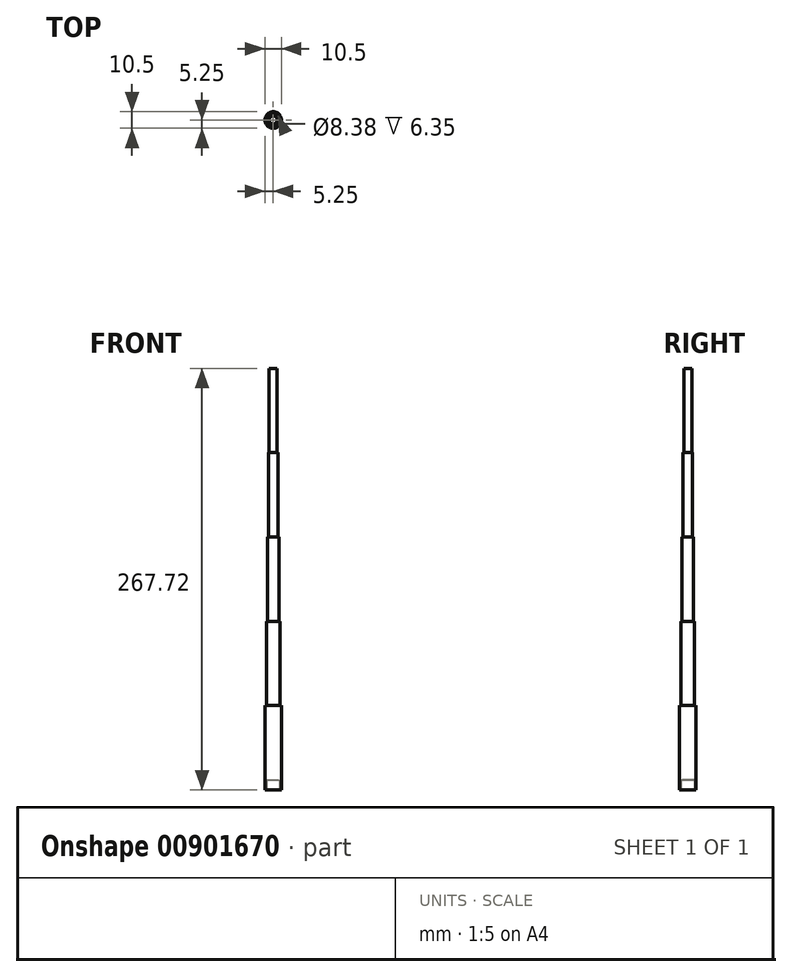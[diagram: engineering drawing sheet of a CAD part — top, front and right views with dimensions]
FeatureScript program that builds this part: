
annotation { "Feature Type Name" : "Feature", "Feature Type Description" : "" }
export const myFeature = defineFeature(function(context is Context, id is Id, definition is map)
    precondition{}
    {
        {
            var Q0;
            Q0=qCreatedBy(makeId("Top.planeOp"),FACE);
            var sketch = newSketch(context, id + "F0", { "sketchPlane" : qUnion([Q0])});
            skCircle(sketch, "E0", {"center": v(0, 0) * mm, "radius": 5.25 * mm});
            skSolve(sketch);
        }
        {
            var Q0;
            Q0=makeQuery(id+"F0.imprint","IMPRINT",FACE,{"disambiguationData":[TD([[makeQuery(id+"F0.imprint","IMPRINT",EDGE,{"derivedFrom":sQuery(id+"F0.wireOp",EDGE,"E0")}),1.0]])]});
            extrude(context, id + "F1", {"entities" : qUnion([Q0]), "depth" : 53.54 * mm, "offsetDistance" : 25.4 * mm});
        }
        {
            var Q0;
            Q0=makeQuery(id+"F1.opExtrude","CAP_FACE",FACE,{"disambiguationData":[OSD([sQuery(id+"F0.wireOp",EDGE,"E0")])],"isStart":true});
            var sketch = newSketch(context, id + "F2", { "sketchPlane" : qUnion([Q0])});
            skCircle(sketch, "E1", {"center": v(0, 0) * mm, "radius": 4.2 * mm});
            skSolve(sketch);
        }
        {
            var Q0;
            Q0=makeQuery(id+"F2.imprint","IMPRINT",FACE,{"disambiguationData":[TD([[makeQuery(id+"F2.imprint","IMPRINT",EDGE,{"derivedFrom":sQuery(id+"F2.wireOp",EDGE,"E1")}),1.0]])]});
            extrude(context, id + "F3", {"entities" : qUnion([Q0]), "operationType" : NewBodyOperationType.REMOVE, "oppositeDirection" : true, "depth" : 6.35 * mm, "offsetDistance" : 25.4 * mm});
        }
        {
            var Q0;
            Q0=makeQuery(id+"F1.opExtrude","CAP_FACE",FACE,{"disambiguationData":[OSD([sQuery(id+"F0.wireOp",EDGE,"E0")])],"isStart":false});
            var sketch = newSketch(context, id + "F4", { "sketchPlane" : qUnion([Q0])});
            skCircle(sketch, "E2", {"center": v(0, 0) * mm, "radius": 4.37 * mm});
            skSolve(sketch);
        }
        {
            var Q0;
            Q0=makeQuery(id+"F4.imprint","IMPRINT",FACE,{"disambiguationData":[TD([[makeQuery(id+"F4.imprint","IMPRINT",EDGE,{"derivedFrom":sQuery(id+"F4.wireOp",EDGE,"E2")}),1.0]])]});
            extrude(context, id + "F5", {"entities" : qUnion([Q0]), "operationType" : NewBodyOperationType.ADD, "depth" : 53.54 * mm, "offsetDistance" : 25.4 * mm});
        }
        {
            var Q0;
            Q0=makeQuery(id+"F5.opExtrude","CAP_FACE",FACE,{"disambiguationData":[OSD([sQuery(id+"F4.wireOp",EDGE,"E2")])],"isStart":false});
            var sketch = newSketch(context, id + "F6", { "sketchPlane" : qUnion([Q0])});
            skCircle(sketch, "E3", {"center": v(0, 0) * mm, "radius": 3.65 * mm});
            skSolve(sketch);
        }
        {
            var Q0;
            Q0=makeQuery(id+"F6.imprint","IMPRINT",FACE,{"disambiguationData":[TD([[makeQuery(id+"F6.imprint","IMPRINT",EDGE,{"derivedFrom":sQuery(id+"F6.wireOp",EDGE,"E3")}),1.0]])]});
            extrude(context, id + "F7", {"entities" : qUnion([Q0]), "operationType" : NewBodyOperationType.ADD, "depth" : 53.54 * mm, "offsetDistance" : 25.4 * mm});
        }
        {
            var Q0;
            Q0=makeQuery(id+"F7.opExtrude","CAP_FACE",FACE,{"disambiguationData":[OSD([sQuery(id+"F6.wireOp",EDGE,"E3")])],"isStart":false});
            var sketch = newSketch(context, id + "F8", { "sketchPlane" : qUnion([Q0])});
            skCircle(sketch, "E4", {"center": v(0, 0) * mm, "radius": 3.05 * mm});
            skSolve(sketch);
        }
        {
            var Q0;
            Q0=makeQuery(id+"F8.imprint","IMPRINT",FACE,{"disambiguationData":[TD([[makeQuery(id+"F8.imprint","IMPRINT",EDGE,{"derivedFrom":sQuery(id+"F8.wireOp",EDGE,"E4")}),1.0]])]});
            extrude(context, id + "F9", {"entities" : qUnion([Q0]), "operationType" : NewBodyOperationType.ADD, "depth" : 53.54 * mm, "offsetDistance" : 25.4 * mm});
        }
        {
            var Q0;
            Q0=makeQuery(id+"F9.opExtrude","CAP_FACE",FACE,{"disambiguationData":[OSD([sQuery(id+"F8.wireOp",EDGE,"E4")])],"isStart":false});
            var sketch = newSketch(context, id + "F10", { "sketchPlane" : qUnion([Q0])});
            skCircle(sketch, "E5", {"center": v(0, 0) * mm, "radius": 2.54 * mm});
            skSolve(sketch);
        }
        {
            var Q0;
            Q0 = qSketchRegion(id + "F10", true);
            extrude(context, id + "F11", {"entities" : qUnion([Q0]), "operationType" : NewBodyOperationType.ADD, "depth" : 53.54 * mm, "offsetDistance" : 25.4 * mm});
        }
    });
